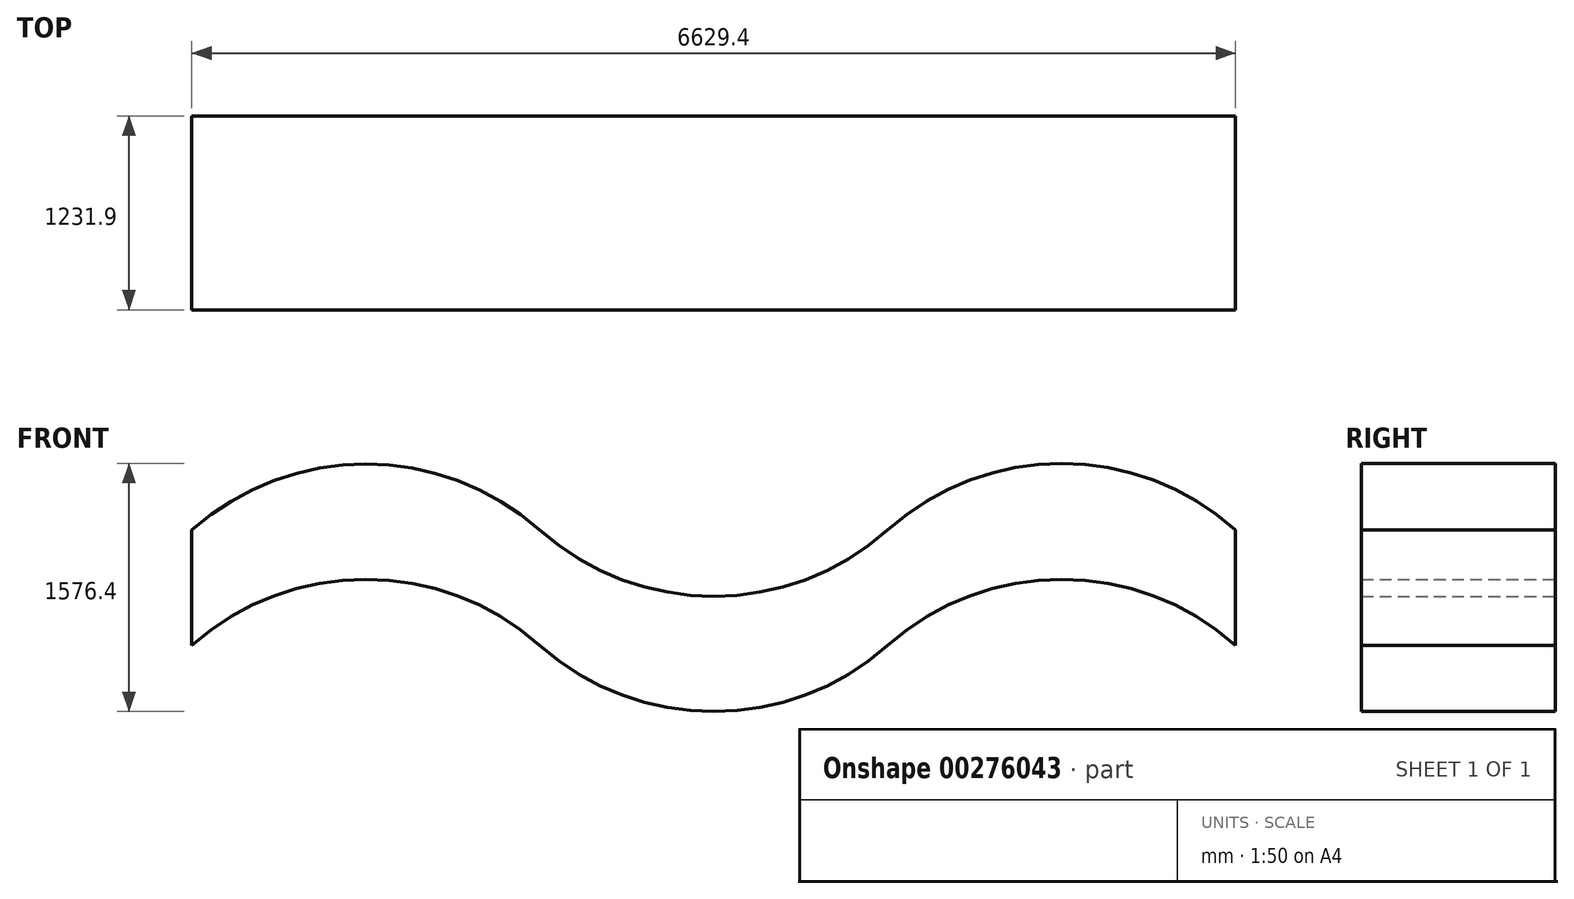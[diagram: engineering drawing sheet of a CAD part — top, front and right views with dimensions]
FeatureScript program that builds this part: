
annotation { "Feature Type Name" : "Feature", "Feature Type Description" : "" }
export const myFeature = defineFeature(function(context is Context, id is Id, definition is map)
    precondition{}
    {
        {
            var Q0;
            Q0=qCreatedBy(makeId("Front.planeOp"),FACE);
            var sketch = newSketch(context, id + "F0", { "sketchPlane" : qUnion([Q0])});
            skLineSegment(sketch, "E0", {"start": v(0, 0) * mm, "end": v(2209.8, 0) * mm});
            skLineSegment(sketch, "E1", {"start": v(2209.8, 0) * mm, "end": v(0, 0) * mm});
            skLineSegment(sketch, "E2", {"start": v(-2209.8, 0) * mm, "end": v(0, 0) * mm});
            skLineSegment(sketch, "E3", {"start": v(-2209.8, 0) * mm, "end": v(-4419.6, 0) * mm});
            skLineSegment(sketch, "E4", {"start": v(-4419.6, 0) * mm, "end": v(-4419.6, 732.3) * mm});
            skLineSegment(sketch, "E5", {"start": v(-2209.8, 0) * mm, "end": v(-2209.8, 732.3) * mm});
            skLineSegment(sketch, "E6", {"start": v(0, 0) * mm, "end": v(0, 732.3) * mm});
            skLineSegment(sketch, "E7", {"start": v(2209.8, 0) * mm, "end": v(2209.8, 732.3) * mm});
            skArc(sketch, "E8", {"start": v(-2209.8, 732.3) * mm, "mid": v(-3314.7, 1152.18) * mm, "end": v(-4419.6, 732.3) * mm});
            skArc(sketch, "E9", {"start": v(-2209.8, 0) * mm, "mid": v(-3314.7, 419.88) * mm, "end": v(-4419.6, 0) * mm});
            skArc(sketch, "E10", {"start": v(-2209.8, 0) * mm, "mid": v(-1104.9, -419.88) * mm, "end": v(0, 0) * mm});
            skArc(sketch, "E11", {"start": v(-2209.8, 732.3) * mm, "mid": v(-1104.9, 312.42) * mm, "end": v(0, 732.3) * mm});
            skArc(sketch, "E12", {"start": v(2209.8, 732.3) * mm, "mid": v(1104.9, 1156.52) * mm, "end": v(0, 732.3) * mm});
            skArc(sketch, "E13", {"start": v(2209.8, 0) * mm, "mid": v(1104.9, 419.88) * mm, "end": v(0, 0) * mm});
            skSolve(sketch);
        }
        {
            var Q0;
            Q0=makeQuery(id+"F0.imprint","IMPRINT",FACE,{"disambiguationData":[TD([[makeQuery(id+"F0.imprint","IMPRINT",EDGE,{"derivedFrom":sQuery(id+"F0.wireOp",EDGE,"E4")}),-1.0]])]});
            var Q1;
            Q1=makeQuery(id+"F0.imprint","IMPRINT",FACE,{"disambiguationData":[TD([[makeQuery(id+"F0.imprint","IMPRINT",EDGE,{"derivedFrom":sQuery(id+"F0.wireOp",EDGE,"E2")}),1.0]])]});
            var Q2;
            Q2=makeQuery(id+"F0.imprint","IMPRINT",FACE,{"disambiguationData":[TD([[makeQuery(id+"F0.imprint","IMPRINT",EDGE,{"derivedFrom":sQuery(id+"F0.wireOp",EDGE,"E2")}),-1.0]])]});
            var Q3;
            Q3=makeQuery(id+"F0.imprint","IMPRINT",FACE,{"disambiguationData":[TD([[makeQuery(id+"F0.imprint","IMPRINT",EDGE,{"derivedFrom":sQuery(id+"F0.wireOp",EDGE,"E6")}),-1.0]])]});
            extrude(context, id + "F1", {"entities" : qUnion([Q0, Q1, Q2, Q3]), "depth" : 1231.9 * mm});
        }
    });
